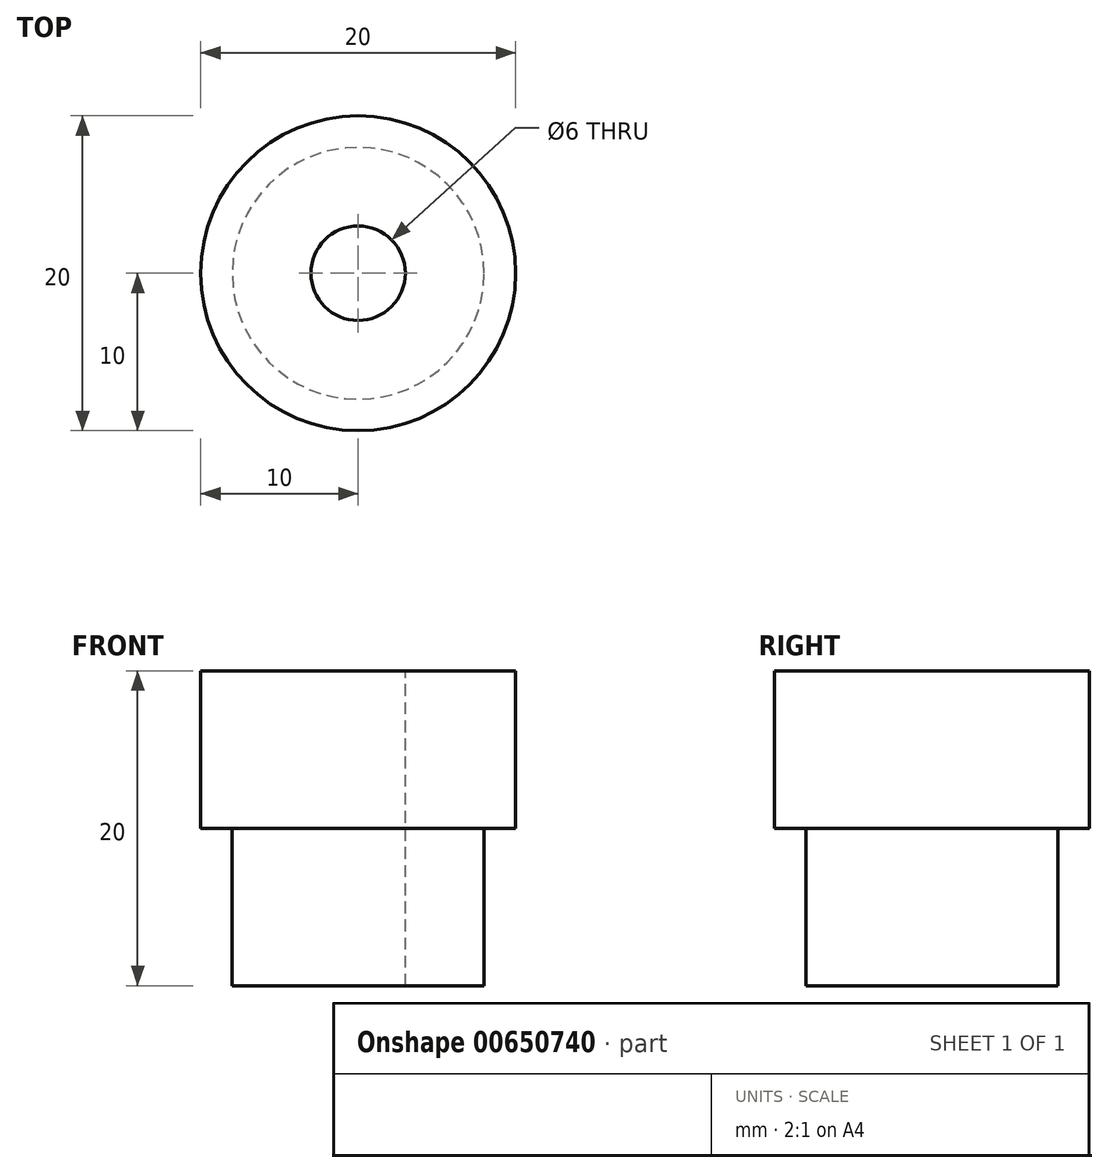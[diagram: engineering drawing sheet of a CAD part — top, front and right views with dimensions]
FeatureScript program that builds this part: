
annotation { "Feature Type Name" : "Feature", "Feature Type Description" : "" }
export const myFeature = defineFeature(function(context is Context, id is Id, definition is map)
    precondition{}
    {
        {
            var Q0;
            Q0=qCreatedBy(makeId("Front.planeOp"),FACE);
            var sketch = newSketch(context, id + "F0", { "sketchPlane" : qUnion([Q0])});
            skLineSegment(sketch, "E0", {"start": v(0, 19.62) * mm, "end": v(0, -16.09) * mm, "construction": true});
            skLineSegment(sketch, "E1", {"start": v(0, -20) * mm, "end": v(-8, -20) * mm});
            skLineSegment(sketch, "E2", {"start": v(-8, -20) * mm, "end": v(-8, -10) * mm});
            skLineSegment(sketch, "E3", {"start": v(-8, -10) * mm, "end": v(-10, -10) * mm});
            skLineSegment(sketch, "E4", {"start": v(-10, -10) * mm, "end": v(-10, 0) * mm});
            skLineSegment(sketch, "E5", {"start": v(-10, 0) * mm, "end": v(0, 0) * mm});
            skLineSegment(sketch, "E6", {"start": v(0, 0) * mm, "end": v(0, -20) * mm});
            skLineSegment(sketch, "E7", {"start": v(-3, 0) * mm, "end": v(-3, -20) * mm});
            skSolve(sketch);
        }
        {
            var Q0;
            {var subQ1=sQuery(id+"F0.wireOp",EDGE,"E2");Q0=makeQuery(id+"F0.imprint","IMPRINT",FACE,{"disambiguationData":[TD([[makeQuery(id+"F0.imprint","IMPRINT",EDGE,{"derivedFrom":subQ1}),-1.0]])]});}
            var Q1;
            Q1=sQuery(id+"F0.wireOp",EDGE,"E6");
            revolve(context, id + "F1", {"entities" : qUnion([Q0]), "axis" : qUnion([Q1]), "revolveType" : RevolveType.FULL});
        }
    });
